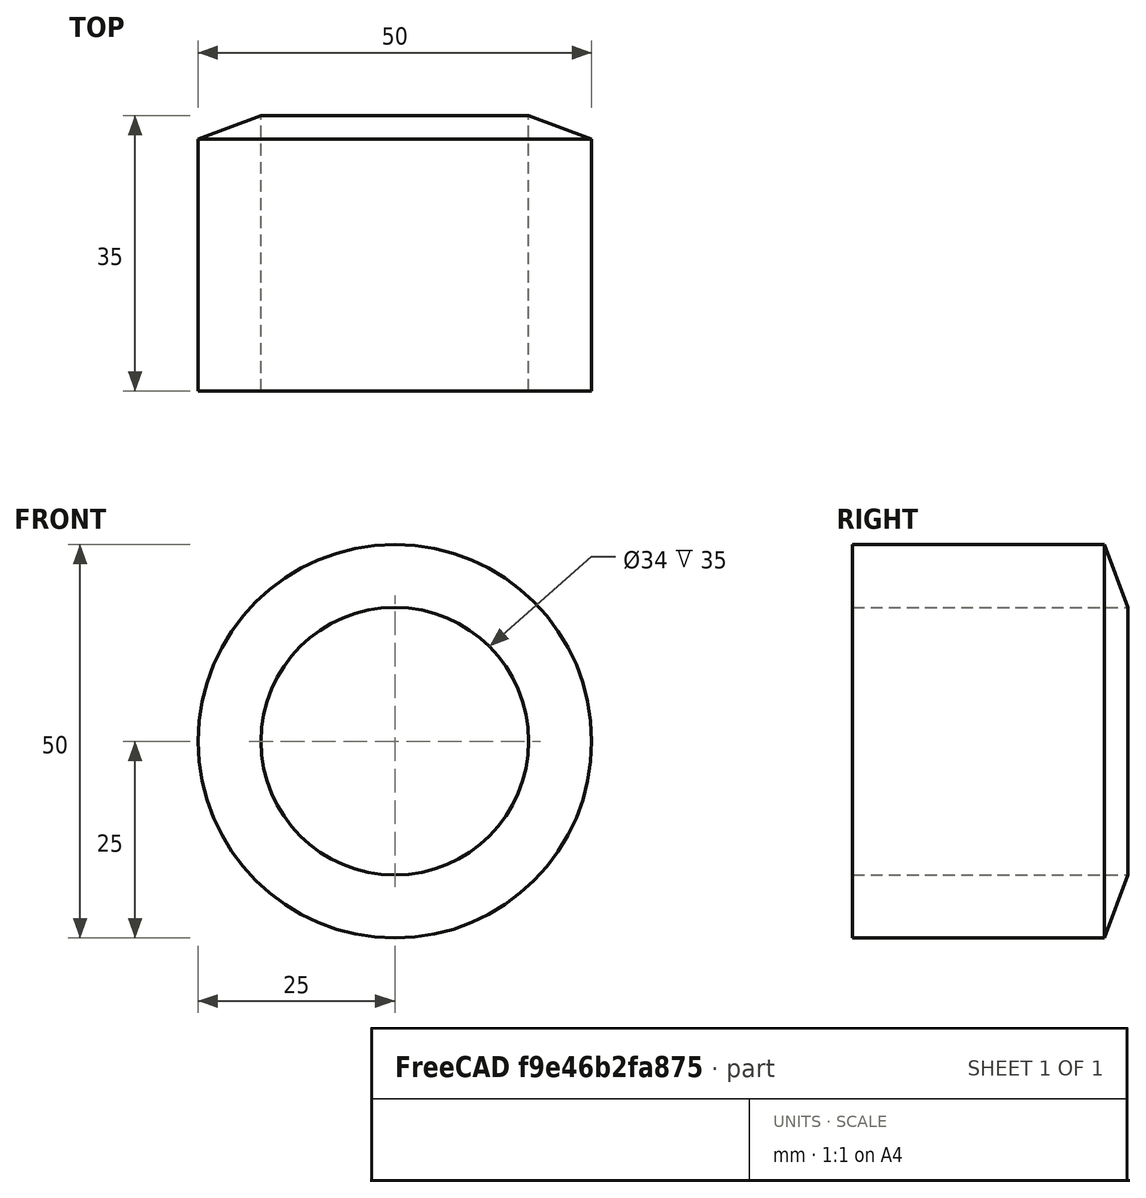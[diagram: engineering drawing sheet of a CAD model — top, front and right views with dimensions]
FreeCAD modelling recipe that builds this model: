
FCSTD DOCUMENT
Label: centreled
objects: Sketcher::SketchObject×1, Part::Revolution×1
note: 2 computed .brp shape members not serialized (recipe doc carries the construction recipe); baked Part::Feature solids carry a one-line shape summary decoded from their .brp

FEATURE [Sketcher::SketchObject] Sketch
  sketch-geometry (4):
    g0: LineSegment StartX=17 StartY=0 StartZ=0 EndX=25 EndY=0 EndZ=0
    g1: LineSegment StartX=17 StartY=0 StartZ=0 EndX=17 EndY=35 EndZ=0
    g2: LineSegment StartX=25 StartY=0 StartZ=0 EndX=25 EndY=32 EndZ=0
    g3: LineSegment StartX=17 StartY=35 StartZ=0 EndX=25 EndY=32 EndZ=0
  constraints (12):
    c: PointOnObject(g0,g-1)
    c: Horizontal(g0)
    c: Vertical(g1)
    c: Coincident(g2,g0)
    c: Vertical(g2)
    c: Distance(g1) = 35
    c: Distance(g2) = 32
    c: Distance(g0) = 8
    c: Coincident(g3,g1)
    c: DistanceX(g0) = 17
    c: Coincident(g1,g0)
    c: Coincident(g3,g2)
FEATURE [Part::Revolution] Revolve
  Angle = 360
  Axis = (0,1,0)
  Base = (0,0,0)
  Source = -> Sketch
